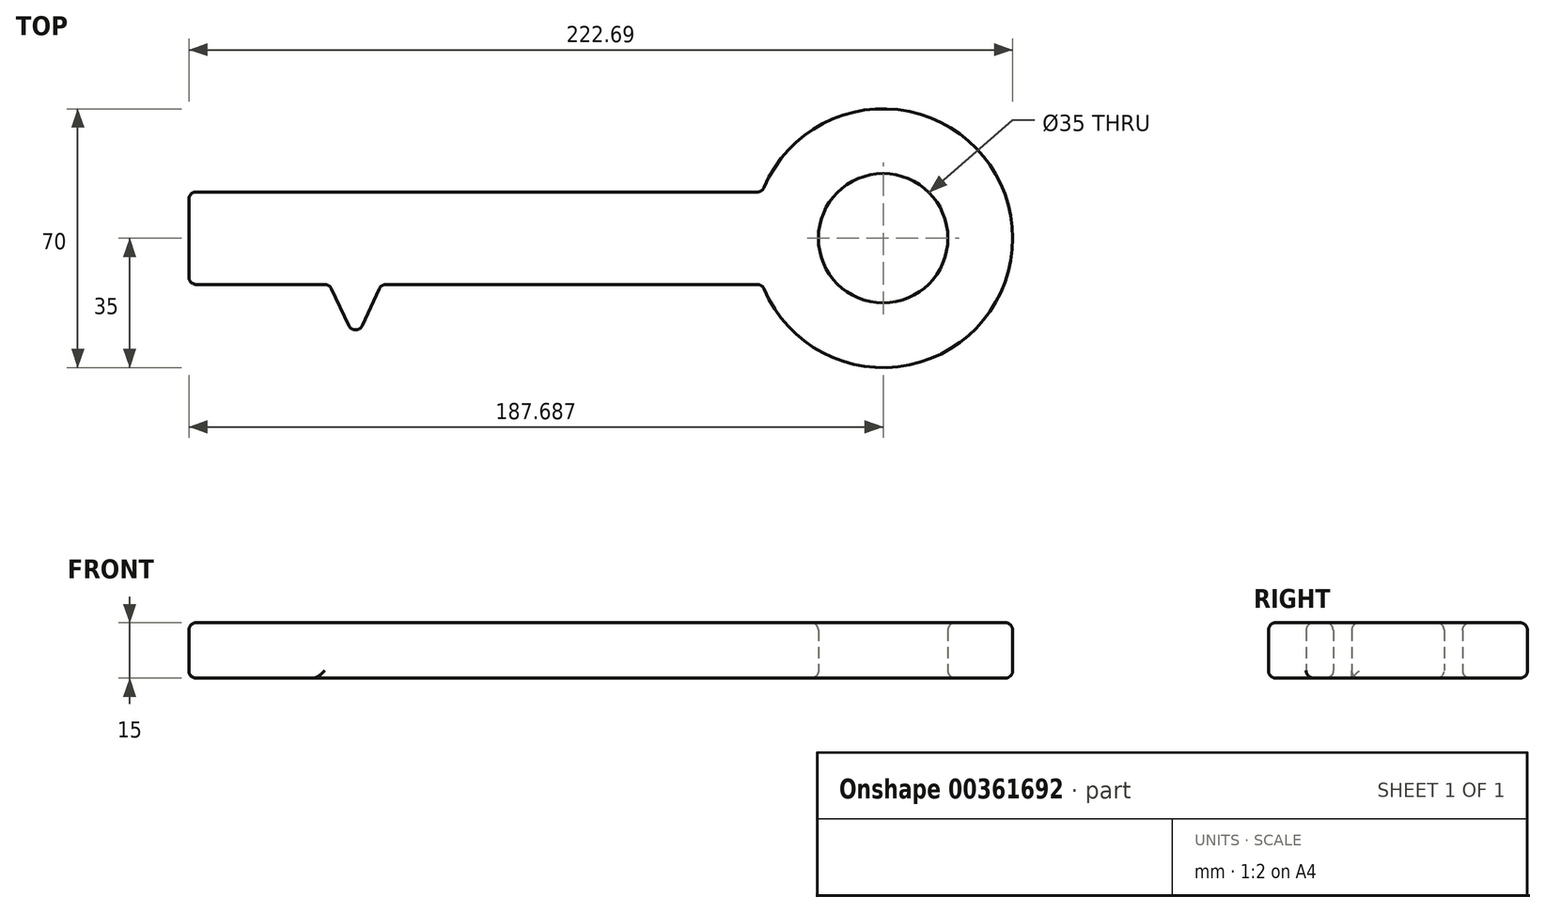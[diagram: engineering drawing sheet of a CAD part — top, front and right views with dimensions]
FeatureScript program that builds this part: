
annotation { "Feature Type Name" : "Feature", "Feature Type Description" : "" }
export const myFeature = defineFeature(function(context is Context, id is Id, definition is map)
    precondition{}
    {
        {
            var Q0;
            Q0=qCreatedBy(makeId("Top.planeOp"),FACE);
            var sketch = newSketch(context, id + "F0", { "sketchPlane" : qUnion([Q0])});
            skLineSegment(sketch, "E0.bottom", {"start": v(-87.13, 58.4) * mm, "end": v(67.87, 58.4) * mm});
            skLineSegment(sketch, "E0.top", {"start": v(-87.13, 33.4) * mm, "end": v(67.87, 33.4) * mm});
            skLineSegment(sketch, "E0.left", {"start": v(-87.13, 58.4) * mm, "end": v(-87.13, 33.4) * mm});
            skLineSegment(sketch, "E1.bottom", {"start": v(-87.13, 33.4) * mm, "end": v(-77.13, 33.4) * mm});
            skLineSegment(sketch, "E1.top", {"start": v(-87.13, 3.4) * mm, "end": v(-77.13, 3.4) * mm});
            skLineSegment(sketch, "E1.left", {"start": v(-87.13, 33.4) * mm, "end": v(-87.13, 3.4) * mm});
            skLineSegment(sketch, "E1.right", {"start": v(-77.13, 33.4) * mm, "end": v(-77.13, 3.4) * mm});
            skLineSegment(sketch, "E2.bottom", {"start": v(-67.13, 33.4) * mm, "end": v(-59.13, 33.4) * mm});
            skLineSegment(sketch, "E2.top", {"start": v(-67.13, 18.4) * mm, "end": v(-59.13, 18.4) * mm});
            skLineSegment(sketch, "E2.left", {"start": v(-67.13, 33.4) * mm, "end": v(-67.13, 18.4) * mm});
            skLineSegment(sketch, "E2.right", {"start": v(-59.13, 33.4) * mm, "end": v(-59.13, 18.4) * mm});
            skLineSegment(sketch, "E3", {"start": v(-49.13, 33.4) * mm, "end": v(-42.05, 18.36) * mm});
            skLineSegment(sketch, "E4", {"start": v(-42.05, 18.36) * mm, "end": v(-35.13, 33.4) * mm});
            skArc(sketch, "E5", {"start": v(67.87, 33.4) * mm, "mid": v(135.56, 45.9) * mm, "end": v(67.87, 58.4) * mm});
            skCircle(sketch, "E6", {"center": v(100.56, 45.9) * mm, "radius": 17.5 * mm});
            skLineSegment(sketch, "E7", {"start": v(100.56, 45.9) * mm, "end": v(-87.13, 45.9) * mm, "construction": true});
            skSolve(sketch);
        }
        {
            var Q0;
            Q0=makeQuery(id+"F0.imprint","IMPRINT",FACE,{"disambiguationData":[TD([[makeQuery(id+"F0.imprint","IMPRINT",EDGE,{"derivedFrom":sQuery(id+"F0.wireOp",EDGE,"E0.bottom")}),-1.0]])]});
            var Q1;
            Q1=makeQuery(id+"F0.imprint","IMPRINT",FACE,{"disambiguationData":[TD([[makeQuery(id+"F0.imprint","IMPRINT",EDGE,{"derivedFrom":sQuery(id+"F0.wireOp",EDGE,"E2.bottom")}),-1.0]])]});
            var Q2;
            {var subQ0=sQuery(id+"F0.wireOp",EDGE,"E3");Q2=makeQuery(id+"F0.imprint","IMPRINT",FACE,{"disambiguationData":[TD([[makeQuery(id+"F0.imprint","IMPRINT",EDGE,{"derivedFrom":subQ0}),1.0]])]});}
            var Q3;
            Q3=makeQuery(id+"F0.imprint","IMPRINT",FACE,{"disambiguationData":[TD([[makeQuery(id+"F0.imprint","IMPRINT",EDGE,{"derivedFrom":sQuery(id+"F0.wireOp",EDGE,"E1.bottom")}),-1.0]])]});
            extrude(context, id + "F1", {"entities" : qUnion([Q0, Q1, Q2, Q3]), "depth" : 15 * mm});
        }
        {
            var Q0;
            {var subQ0=sQuery(id+"F0.wireOp",EDGE,"E0.top");Q0=makeQuery(id+"F1.opExtrude","CAP_EDGE",EDGE,{"disambiguationData":[OSD([subQ0]),TDD([makeQuery(id+"F0.imprint","IMPRINT",EDGE,{"disambiguationData":[TD([[makeQuery(id+"F0.imprint","INTERSECT",VERTEX,{"derivedFrom":[subQ0,sQuery(id+"F0.wireOp",EDGE,"E3")]}),1.0]])],"derivedFrom":subQ0})])],"isStart":false});}
            var Q1;
            Q1=makeQuery(id+"F1.opExtrude","CAP_FACE",FACE,{"disambiguationData":[OSD([sQuery(id+"F0.wireOp",EDGE,"E0.bottom"),sQuery(id+"F0.wireOp",EDGE,"E0.top"),sQuery(id+"F0.wireOp",EDGE,"E0.left"),sQuery(id+"F0.wireOp",EDGE,"E1.top"),sQuery(id+"F0.wireOp",EDGE,"E1.left"),sQuery(id+"F0.wireOp",EDGE,"E1.right"),sQuery(id+"F0.wireOp",EDGE,"E2.top"),sQuery(id+"F0.wireOp",EDGE,"E2.left"),sQuery(id+"F0.wireOp",EDGE,"E2.right"),sQuery(id+"F0.wireOp",EDGE,"E3"),sQuery(id+"F0.wireOp",EDGE,"E4"),sQuery(id+"F0.wireOp",EDGE,"E5"),sQuery(id+"F0.wireOp",EDGE,"E6")])],"isStart":false});
            var Q2;
            Q2=makeQuery(id+"F1.opExtrude","CAP_EDGE",EDGE,{"disambiguationData":[OSD([sQuery(id+"F0.wireOp",EDGE,"E5")])],"isStart":true});
            var Q3;
            Q3=makeQuery(id+"F1.opExtrude","SWEPT_FACE",FACE,{"disambiguationData":[OSD([sQuery(id+"F0.wireOp",EDGE,"E5")])]});
            var Q4;
            Q4=makeQuery(id+"F1.opExtrude","SWEPT_FACE",FACE,{"disambiguationData":[OSD([sQuery(id+"F0.wireOp",EDGE,"E0.bottom")])]});
            var Q5;
            Q5=makeQuery(id+"F1.opExtrude","SWEPT_FACE",FACE,{"disambiguationData":[OSD([sQuery(id+"F0.wireOp",EDGE,"E0.left"),sQuery(id+"F0.wireOp",EDGE,"E1.left")])]});
            var Q6;
            Q6=makeQuery(id+"F1.opExtrude","SWEPT_EDGE",EDGE,{"disambiguationData":[OSD([sQuery(id+"F0.wireOp",EDGE,"E1.top"),sQuery(id+"F0.wireOp",EDGE,"E1.right")])]});
            var Q7;
            Q7=makeQuery(id+"F1.opExtrude","SWEPT_EDGE",EDGE,{"disambiguationData":[OSD([sQuery(id+"F0.wireOp",EDGE,"E2.top"),sQuery(id+"F0.wireOp",EDGE,"E2.right")])]});
            var Q8;
            Q8=makeQuery(id+"F1.opExtrude","SWEPT_FACE",FACE,{"disambiguationData":[OSD([sQuery(id+"F0.wireOp",EDGE,"E3")])]});
            var Q9;
            Q9=makeQuery(id+"F1.opExtrude","SWEPT_EDGE",EDGE,{"disambiguationData":[OSD([sQuery(id+"F0.wireOp",EDGE,"E0.top"),sQuery(id+"F0.wireOp",EDGE,"E4")])]});
            var Q10;
            Q10=makeQuery(id+"F1.opExtrude","SWEPT_FACE",FACE,{"disambiguationData":[OSD([sQuery(id+"F0.wireOp",EDGE,"E1.top")])]});
            var Q11;
            Q11=makeQuery(id+"F1.opExtrude","SWEPT_EDGE",EDGE,{"disambiguationData":[OSD([sQuery(id+"F0.wireOp",EDGE,"E0.top"),sQuery(id+"F0.wireOp",EDGE,"E3")])]});
            var Q12;
            Q12=makeQuery(id+"F1.opExtrude","SWEPT_EDGE",EDGE,{"disambiguationData":[OSD([sQuery(id+"F0.wireOp",EDGE,"E2.top"),sQuery(id+"F0.wireOp",EDGE,"E2.left")])]});
            var Q13;
            Q13=makeQuery(id+"F1.opExtrude","CAP_EDGE",EDGE,{"disambiguationData":[OSD([sQuery(id+"F0.wireOp",EDGE,"E6")])],"isStart":true});
            var Q14;
            Q14=makeQuery(id+"F1.opExtrude","CAP_EDGE",EDGE,{"disambiguationData":[OSD([sQuery(id+"F0.wireOp",EDGE,"E0.bottom")])],"isStart":false});
            var Q15;
            Q15=makeQuery(id+"F1.opExtrude","CAP_EDGE",EDGE,{"disambiguationData":[OSD([sQuery(id+"F0.wireOp",EDGE,"E5")])],"isStart":false});
            var Q16;
            Q16=makeQuery(id+"F1.opExtrude","SWEPT_EDGE",EDGE,{"disambiguationData":[OSD([sQuery(id+"F0.wireOp",EDGE,"E0.top"),sQuery(id+"F0.wireOp",EDGE,"E5")])]});
            var Q17;
            Q17=makeQuery(id+"F1.opExtrude","CAP_EDGE",EDGE,{"disambiguationData":[OSD([sQuery(id+"F0.wireOp",EDGE,"E3")])],"isStart":false});
            var Q18;
            Q18=makeQuery(id+"F1.opExtrude","CAP_EDGE",EDGE,{"disambiguationData":[OSD([sQuery(id+"F0.wireOp",EDGE,"E0.left"),sQuery(id+"F0.wireOp",EDGE,"E1.left")])],"isStart":false});
            var Q19;
            Q19=makeQuery(id+"F1.opExtrude","CAP_EDGE",EDGE,{"disambiguationData":[OSD([sQuery(id+"F0.wireOp",EDGE,"E1.top")])],"isStart":false});
            var Q20;
            Q20=makeQuery(id+"F1.opExtrude","CAP_EDGE",EDGE,{"disambiguationData":[OSD([sQuery(id+"F0.wireOp",EDGE,"E1.top")])],"isStart":true});
            var Q21;
            Q21=makeQuery(id+"F1.opExtrude","CAP_EDGE",EDGE,{"disambiguationData":[OSD([sQuery(id+"F0.wireOp",EDGE,"E1.right")])],"isStart":false});
            var Q22;
            {var subQ0=sQuery(id+"F0.wireOp",EDGE,"E0.top");Q22=makeQuery(id+"F1.opExtrude","CAP_EDGE",EDGE,{"disambiguationData":[OSD([subQ0]),TDD([makeQuery(id+"F0.imprint","IMPRINT",EDGE,{"disambiguationData":[TD([[makeQuery(id+"F0.imprint","INTERSECT",VERTEX,{"derivedFrom":[subQ0,sQuery(id+"F0.wireOp",EDGE,"E1.bottom"),sQuery(id+"F0.wireOp",EDGE,"E1.right")]}),-1.0]])],"derivedFrom":subQ0})])],"isStart":false});}
            var Q23;
            Q23=makeQuery(id+"F1.opExtrude","CAP_EDGE",EDGE,{"disambiguationData":[OSD([sQuery(id+"F0.wireOp",EDGE,"E2.left")])],"isStart":false});
            var Q24;
            Q24=makeQuery(id+"F1.opExtrude","CAP_EDGE",EDGE,{"disambiguationData":[OSD([sQuery(id+"F0.wireOp",EDGE,"E2.top")])],"isStart":true});
            var Q25;
            Q25=makeQuery(id+"F1.opExtrude","SWEPT_EDGE",EDGE,{"disambiguationData":[OSD([sQuery(id+"F0.wireOp",EDGE,"E3"),sQuery(id+"F0.wireOp",EDGE,"E4")])]});
            var Q26;
            Q26=makeQuery(id+"F1.opExtrude","CAP_EDGE",EDGE,{"disambiguationData":[OSD([sQuery(id+"F0.wireOp",EDGE,"E4")])],"isStart":true});
            var Q27;
            {var subQ0=sQuery(id+"F0.wireOp",EDGE,"E0.top");Q27=makeQuery(id+"F1.opExtrude","CAP_EDGE",EDGE,{"disambiguationData":[OSD([subQ0]),TDD([makeQuery(id+"F0.imprint","IMPRINT",EDGE,{"disambiguationData":[TD([[makeQuery(id+"F0.imprint","INTERSECT",VERTEX,{"derivedFrom":[subQ0,sQuery(id+"F0.wireOp",EDGE,"E5")]}),1.0]])],"derivedFrom":subQ0})])],"isStart":false});}
            var Q28;
            {var subQ0=sQuery(id+"F0.wireOp",EDGE,"E0.top");Q28=makeQuery(id+"F1.opExtrude","CAP_EDGE",EDGE,{"disambiguationData":[OSD([subQ0]),TDD([makeQuery(id+"F0.imprint","IMPRINT",EDGE,{"disambiguationData":[TD([[makeQuery(id+"F0.imprint","INTERSECT",VERTEX,{"derivedFrom":[subQ0,sQuery(id+"F0.wireOp",EDGE,"E5")]}),1.0]])],"derivedFrom":subQ0})])],"isStart":true});}
            var Q29;
            Q29=makeQuery(id+"F1.opExtrude","CAP_EDGE",EDGE,{"disambiguationData":[OSD([sQuery(id+"F0.wireOp",EDGE,"E0.bottom")])],"isStart":true});
            fillet(context, id + "F2", {"entities" : qUnion([Q0, Q1, Q2, Q3, Q4, Q5, Q6, Q7, Q8, Q9, Q10, Q11, Q12, Q13, Q14, Q15, Q16, Q17, Q18, Q19, Q20, Q21, Q22, Q23, Q24, Q25, Q26, Q27, Q28, Q29]), "radius" : 2 * mm, "tangentPropagation" : true, "allowEdgeOverflow" : false});
        }
    });
